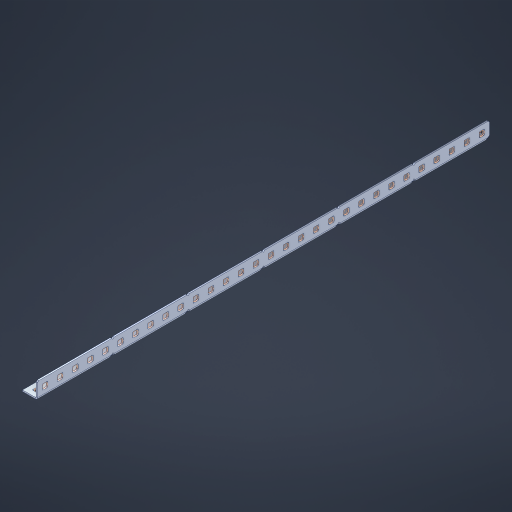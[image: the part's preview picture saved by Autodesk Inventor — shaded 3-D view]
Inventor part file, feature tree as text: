
AUTODESK INVENTOR PART (.ipt)
format: ipt  version: 2023 (Build 270158000, 158)  size: 956,416 bytes
history: native  units: in
note: dims shown in document units (in); Inventor stores cm internally (conversion verified against a paired STEP export)
features: other x65, extrude x59, sheet_metal_op x10, sketch x8, mirror x1, pattern_linear x1, chamfer x1
ambient origin geometry x8: Origin, YZ Plane, XZ Plane, XY Plane, X Axis, Y Axis, Z Axis, Center Point
bodies: Solid1 (feature_tree), Body (feature_tree)
feature tree (145):
  other  "Flange Pattern Plane"
  sheet_metal_op  "Flange Pattern"
  sheet_metal_op  "Body Pattern"
  other  "Arc Length"
  mirror  "Notch Mirror"
  pattern_linear  "Notch Pattern"  Spacing1=0.1875in  [1 undecoded]
  chamfer  "End Chamfer"
  extrude  "Half Cut"  Depth=0.0469in
  sketch  "Sketch1"  dims[d0=2.5in]
  other  "Plate1"
  sketch  "Sketch2"  dims[d1=15.0in]
  other  "Plate2"
  sheet_metal_op  "Bend1"
  sheet_metal_op  "Corner1"
  sketch  "Sketch3"  dims[d2=0.0469in]
  other  "Flange Pattern Sketch"
  sketch  "Sketch7"  dims[d3=0.0469in]
  other  "Srf1"
  other  "Srf2"
  sketch  "Sketch8"  dims[d4=0.0234in]
  sketch  "Sketch9"  dims[d5=0.0938in]
  other  "Srf91"
  sheet_metal_op  "Body Pattern Sketch"
  other  "Srf92"
  sketch  "Sketch13"  dims[d6=0.0469in]
  sketch  "Sketch14"  dims[d7=0.5in d8=90.0deg d9=0.0312in d10=0.1875in d11=0.0469in d12=0.0469in d16=0.182in d17=0.02in d18=0.0469in d19=0.0in d20=0.25in d21=0.25in d46=0.172in d47=1.0in d48=0.0in d49=0.182in d50=0.02in d51=0.25in d52=0.25in d53=0.0469in d54=0.0in d55=0.172in d56=1.0in d57=0.0in d60=11.811in d62=0.5in d63=0.3937in d65=0.5in d85=0.1227in d86=0.1659in d88=0.04in d89=0.0469in d90=0.0in d91=0.04in d92=0.0491in d95=2.5in d96=0.04in d97=0.25in d98=45.0deg d101=0.0in d102=2.497in d131=0.5in d132=11.811in d134=0.5in d139=0.5in]
  other  "Srf856"
  other  "Srf1310"
  other  "Srf1311"
  other  "Srf1312"
  other  "Srf1376"
  other  "Srf1377"
  other  "Srf1728"
  other  "Srf1755"
  other  "Srf1878"
  other  "Srf1879"
  other  "Srf1880"
  other  "Srf1881"
  other  "Srf1882"
  other  "Srf1883"
  other  "Srf1884"
  other  "Srf1885"
  other  "Srf1886"
  other  "Srf1887"
  other  "Srf1888"
  other  "Srf1889"
  other  "Srf1890"
  other  "Srf1891"
  other  "Srf1892"
  other  "Srf1893"
  other  "Srf1894"
  other  "Srf1895"
  other  "Srf1896"
  other  "Srf1897"
  other  "Srf1898"
  other  "Srf1899"
  other  "Srf1900"
  other  "Srf1901"
  other  "Srf1942"
  other  "Srf1943"
  other  "Srf1944"
  other  "Srf1945"
  other  "Srf1946"
  other  "Srf1947"
  other  "Srf1948"
  other  "Srf1949"
  other  "Srf1950"
  other  "Srf1951"
  other  "Srf1952"
  other  "Srf1953"
  other  "Srf1954"
  other  "Srf1955"
  other  "Srf1956"
  other  "Srf1957"
  other  "Srf1958"
  other  "Srf1959"
  other  "Srf1960"
  other  "Srf1961"
  other  "Srf1962"
  other  "Srf1963"
  other  "Srf1964"
  other  "Srf1965"
  sheet_metal_op  "Flange Stamp"
  sheet_metal_op  "Flange Circle"
  sheet_metal_op  "Body Stamp"
  sheet_metal_op  "Body Circle"
  sheet_metal_op  "Notch"
  extrude  "ExtrusionSrf2"  Depth=0.0469in
  extrude  "ExtrusionSrf92"  Depth=0.5in
  extrude  "ExtrusionSrf856"  Depth=0.02in
  extrude  "ExtrusionSrf1310"  Depth=0.0469in
  extrude  "ExtrusionSrf1311"  TaperAngle=0.0deg  [1 undecoded]
  extrude  "ExtrusionSrf1312"  Depth=0.5in
  extrude  "ExtrusionSrf1376"  Depth=0.5in
  extrude  "ExtrusionSrf1377"  Depth=0.5in
  extrude  "ExtrusionSrf1728"  Depth=0.5in TaperAngle=0.0deg
  extrude  "ExtrusionSrf1755"  Depth=0.5in
  extrude  "ExtrusionSrf1878"  Depth=0.02in
  extrude  "ExtrusionSrf1879"  Depth=0.5in
  extrude  "ExtrusionSrf1880"  Depth=0.5in
  extrude  "ExtrusionSrf1881"  Depth=0.0469in
  extrude  "ExtrusionSrf1882"  TaperAngle=0.0deg  [1 undecoded]
  extrude  "ExtrusionSrf1883"  Depth=0.5in
  extrude  "ExtrusionSrf1884"  Depth=0.5in TaperAngle=0.0deg
  extrude  "ExtrusionSrf1885"  Depth=0.5in
  extrude  "ExtrusionSrf1886"  Depth=0.5in
  extrude  "ExtrusionSrf1887"  Depth=0.5in
  extrude  "ExtrusionSrf1888"  Depth=0.5in
  extrude  "ExtrusionSrf1889"  Depth=0.5in
  extrude  "ExtrusionSrf1890"  Depth=0.0469in
  extrude  "ExtrusionSrf1891"  TaperAngle=0.0deg  [1 undecoded]
  extrude  "ExtrusionSrf1892"  Depth=0.5in
  extrude  "ExtrusionSrf1893"  Depth=0.5in
  extrude  "ExtrusionSrf1894"  Depth=0.5in
  extrude  "ExtrusionSrf1895"  Depth=0.5in TaperAngle=45.0deg
  extrude  "ExtrusionSrf1896"  TaperAngle=0.0deg  [1 undecoded]
  extrude  "ExtrusionSrf1897"  Depth=0.5in
  extrude  "ExtrusionSrf1898"  Depth=0.5in
  extrude  "ExtrusionSrf1899"  Depth=0.5in
  extrude  "ExtrusionSrf1900"  Depth=0.5in
  extrude  "ExtrusionSrf1901"  Depth=0.5in
  extrude  "ExtrusionSrf1942"  [1 undecoded]
  extrude  "ExtrusionSrf1943"  [1 undecoded]
  extrude  "ExtrusionSrf1944"  [1 undecoded]
  extrude  "ExtrusionSrf1945"  [1 undecoded]
  extrude  "ExtrusionSrf1946"  [1 undecoded]
  extrude  "ExtrusionSrf1947"  [1 undecoded]
  extrude  "ExtrusionSrf1948"  [1 undecoded]
  extrude  "ExtrusionSrf1949"  [1 undecoded]
  extrude  "ExtrusionSrf1950"  [1 undecoded]
  extrude  "ExtrusionSrf1951"  [1 undecoded]
  extrude  "ExtrusionSrf1952"  [1 undecoded]
  extrude  "ExtrusionSrf1953"  [1 undecoded]
  extrude  "ExtrusionSrf1954"  [1 undecoded]
  extrude  "ExtrusionSrf1955"  [1 undecoded]
  extrude  "ExtrusionSrf1956"  [1 undecoded]
  extrude  "ExtrusionSrf1957"  [1 undecoded]
  extrude  "ExtrusionSrf1958"  [1 undecoded]
  extrude  "ExtrusionSrf1959"  [1 undecoded]
  extrude  "ExtrusionSrf1960"  [1 undecoded]
  extrude  "ExtrusionSrf1961"  [1 undecoded]
  extrude  "ExtrusionSrf1962"  [1 undecoded]
  extrude  "ExtrusionSrf1963"  [1 undecoded]
  extrude  "ExtrusionSrf1964"  [1 undecoded]
  extrude  "ExtrusionSrf1965"  [1 undecoded]
note: 29 required parameter values undecoded (feature->parameter linkage not recoverable at this tier; creation-order binding heuristic only, values carry confidence <= 0.55)
